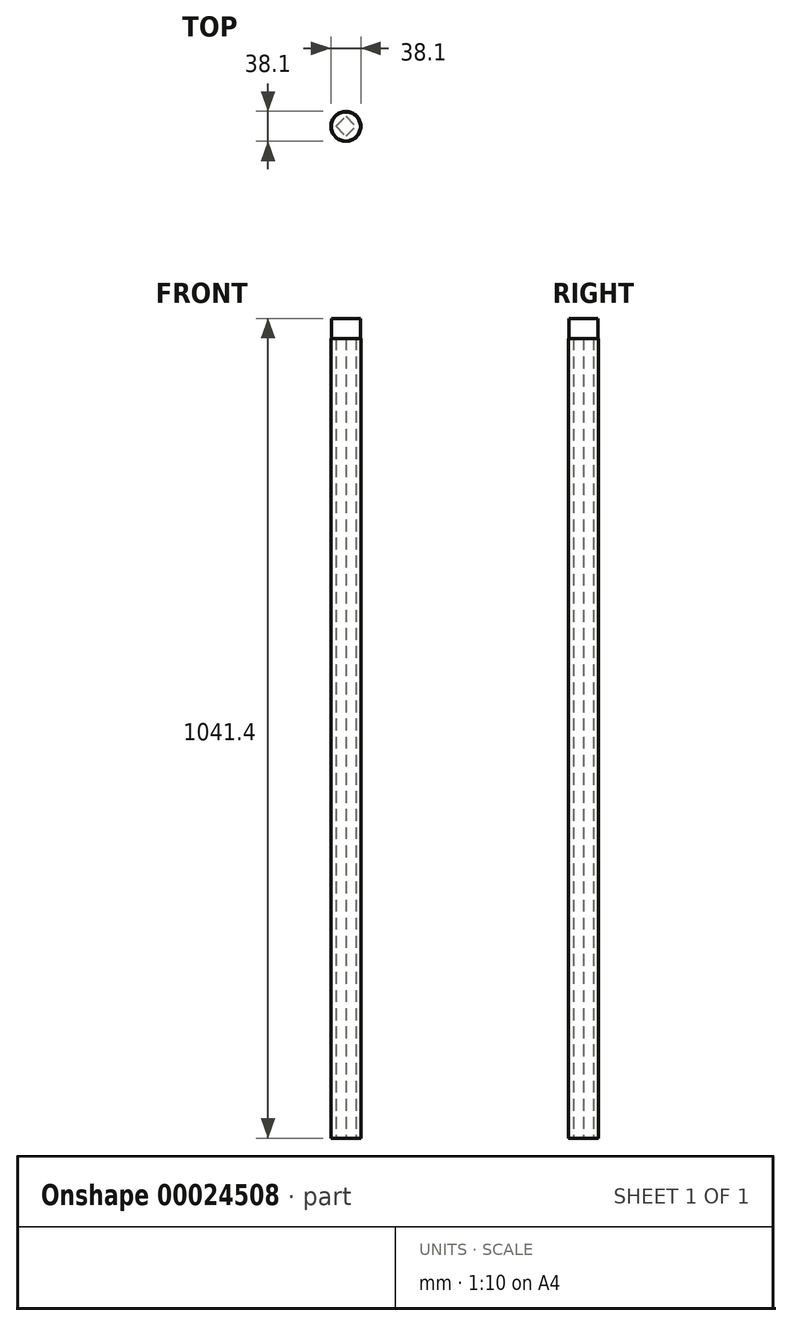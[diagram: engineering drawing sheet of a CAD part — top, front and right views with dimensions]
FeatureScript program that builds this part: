
annotation { "Feature Type Name" : "Feature", "Feature Type Description" : "" }
export const myFeature = defineFeature(function(context is Context, id is Id, definition is map)
    precondition{}
    {
        {
            var Q0;
            Q0=qCreatedBy(makeId("Top.planeOp"),FACE);
            var sketch = newSketch(context, id + "F0", { "sketchPlane" : qUnion([Q0])});
            skLineSegment(sketch, "E0", {"start": v(0, 0) * mm, "end": v(12.7, 12.7) * mm});
            skLineSegment(sketch, "E1", {"start": v(12.7, 12.7) * mm, "end": v(25.4, 0) * mm});
            skLineSegment(sketch, "E2", {"start": v(0, 0) * mm, "end": v(12.7, -12.7) * mm});
            skLineSegment(sketch, "E3", {"start": v(12.7, -12.7) * mm, "end": v(25.4, 0) * mm});
            skCircle(sketch, "E4", {"center": v(12.7, 0) * mm, "radius": 19.05 * mm});
            skSolve(sketch);
        }
        {
            var Q0;
            Q0 = qSketchRegion(id + "F0", true);
            extrude(context, id + "F1", {"entities" : qUnion([Q0]), "depth" : 1016 * mm});
        }
        {
            var Q0;
            Q0=makeQuery(id+"F1.opExtrude","CAP_FACE",FACE,{"disambiguationData":[OSD([sQuery(id+"F0.wireOp",EDGE,"E0"),sQuery(id+"F0.wireOp",EDGE,"E1"),sQuery(id+"F0.wireOp",EDGE,"E2"),sQuery(id+"F0.wireOp",EDGE,"E3"),sQuery(id+"F0.wireOp",EDGE,"E4")])],"isStart":false});
            cPlane(context, id + "F2", {"entities" : qUnion([Q0]), "cplaneType" : CPlaneType.OFFSET, "offset" : 25.4 * mm, "width" : 152.4 * mm, "height" : 152.4 * mm});
        }
        {
            var Q0;
            Q0=qCreatedBy(id+"F2.planeOp",FACE);
            var sketch = newSketch(context, id + "F3", { "sketchPlane" : qUnion([Q0])});
            skCircle(sketch, "E5", {"center": v(12.7, -0.15) * mm, "radius": 18.46 * mm});
            skSolve(sketch);
        }
        {
            var Q0;
            Q0 = qSketchRegion(id + "F3", true);
            extrude(context, id + "F4", {"entities" : qUnion([Q0]), "operationType" : NewBodyOperationType.ADD, "oppositeDirection" : true, "depth" : 25.4 * mm});
        }
    });
